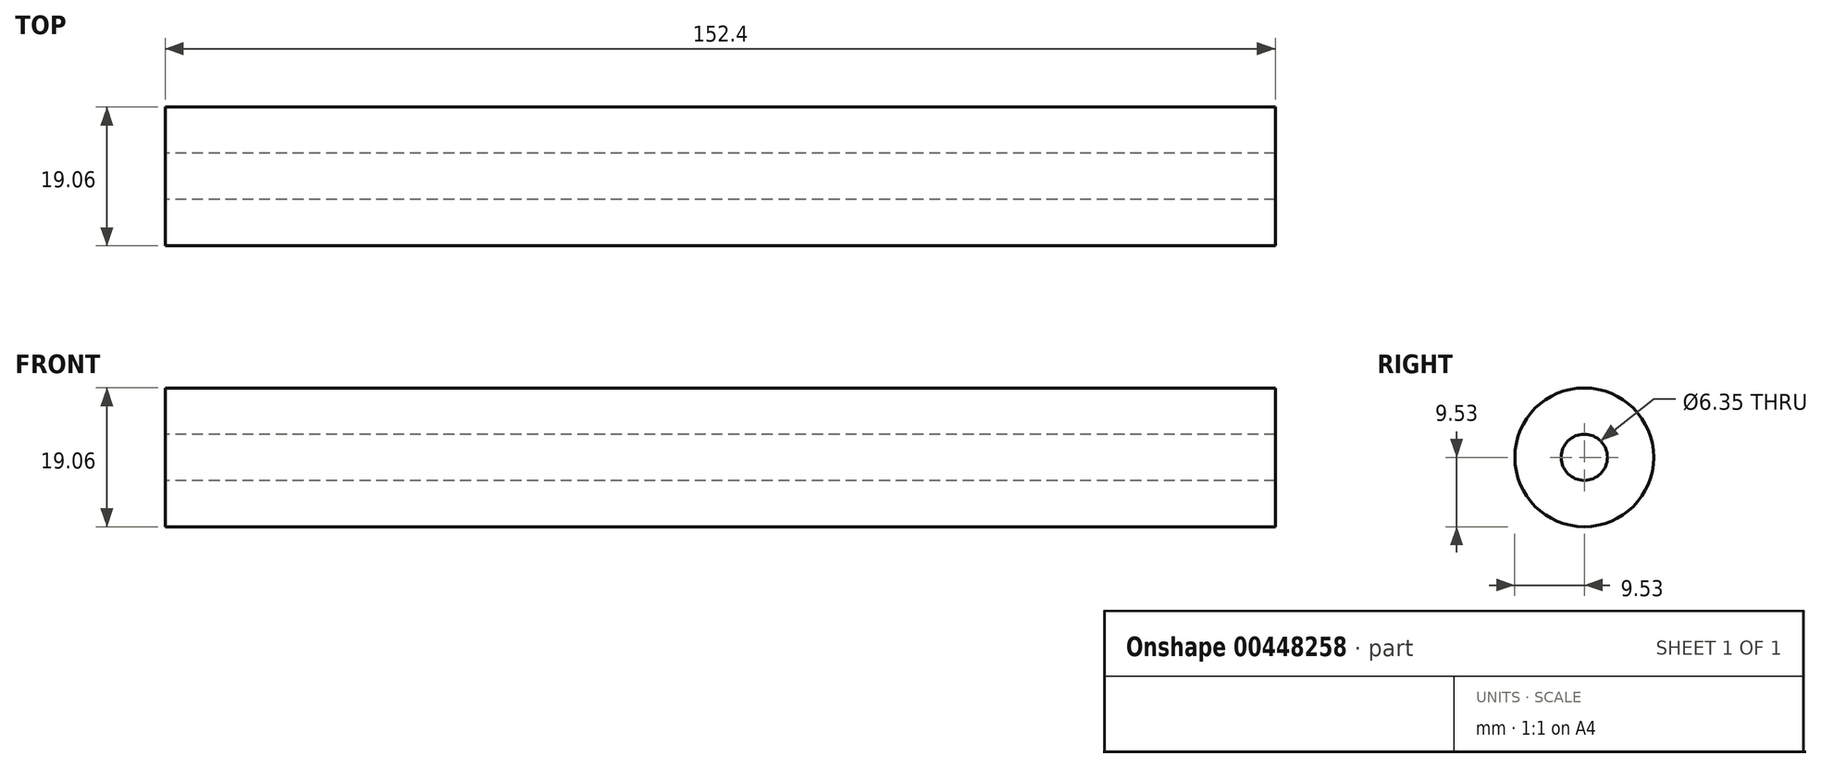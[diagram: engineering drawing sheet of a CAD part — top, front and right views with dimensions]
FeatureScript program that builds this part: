
annotation { "Feature Type Name" : "Feature", "Feature Type Description" : "" }
export const myFeature = defineFeature(function(context is Context, id is Id, definition is map)
    precondition{}
    {
        {
            var Q0;
            Q0=qCreatedBy(makeId("Right.planeOp"),FACE);
            var sketch = newSketch(context, id + "F0", { "sketchPlane" : qUnion([Q0])});
            skCircle(sketch, "E0", {"center": v(0, 0) * mm, "radius": 9.53 * mm});
            skCircle(sketch, "E1", {"center": v(0, 0) * mm, "radius": 3.18 * mm});
            skSolve(sketch);
        }
        {
            var Q0;
            Q0=makeQuery(id+"F0.imprint","IMPRINT",FACE,{"disambiguationData":[TD([[makeQuery(id+"F0.imprint","IMPRINT",EDGE,{"derivedFrom":sQuery(id+"F0.wireOp",EDGE,"E0")}),1.0]])]});
            extrude(context, id + "F1", {"entities" : qUnion([Q0]), "depth" : 152.4 * mm});
        }
    });
